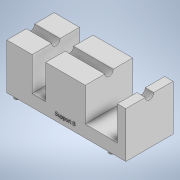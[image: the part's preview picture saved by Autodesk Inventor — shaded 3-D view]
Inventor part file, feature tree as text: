
AUTODESK INVENTOR PART (.ipt)
format: ipt  version: 2021 (Build 250183000, 183)  size: 374,272 bytes
history: native  units: mm
features: sketch x5, extrude x4, emboss x1
ambient origin geometry x8: Origin, YZ Plane, XZ Plane, XY Plane, X Axis, Y Axis, Z Axis, Center Point
bodies: Body1 (feature_tree)
feature tree (10):
  extrude  "Extrusion3"  Depth=28.024mm
  extrude  "Extrusion4"  Depth=27.147mm TaperAngle=0.0deg
  extrude  "Extrusion5"  Depth=15.0mm
  extrude  "Extrusion6"  Depth=46.5mm
  emboss  "Emboss1"
  sketch  "Sketch7"  dims[d32=70.5mm d34=28.024mm]
  sketch  "Sketch8"  dims[d35=14.012mm d37=27.147mm d38=0.0mm]
  sketch  "Sketch9"  dims[d39=20.0mm d40=15.0mm]
  sketch  "Sketch10"  dims[d41=8.0mm d42=46.5mm]
  sketch  "Sketch11"  dims[d44=5.0mm d45=0.0mm d46=0.0mm d47=5.0mm d48=0.0mm d49=0.0mm d50=3.0mm d51=2.5mm d52=3.0mm d54=3.0mm d55=0.0mm d56=56.0mm d57=3.5mm d58=3.5mm d59=1.0mm d60=0.0mm]
